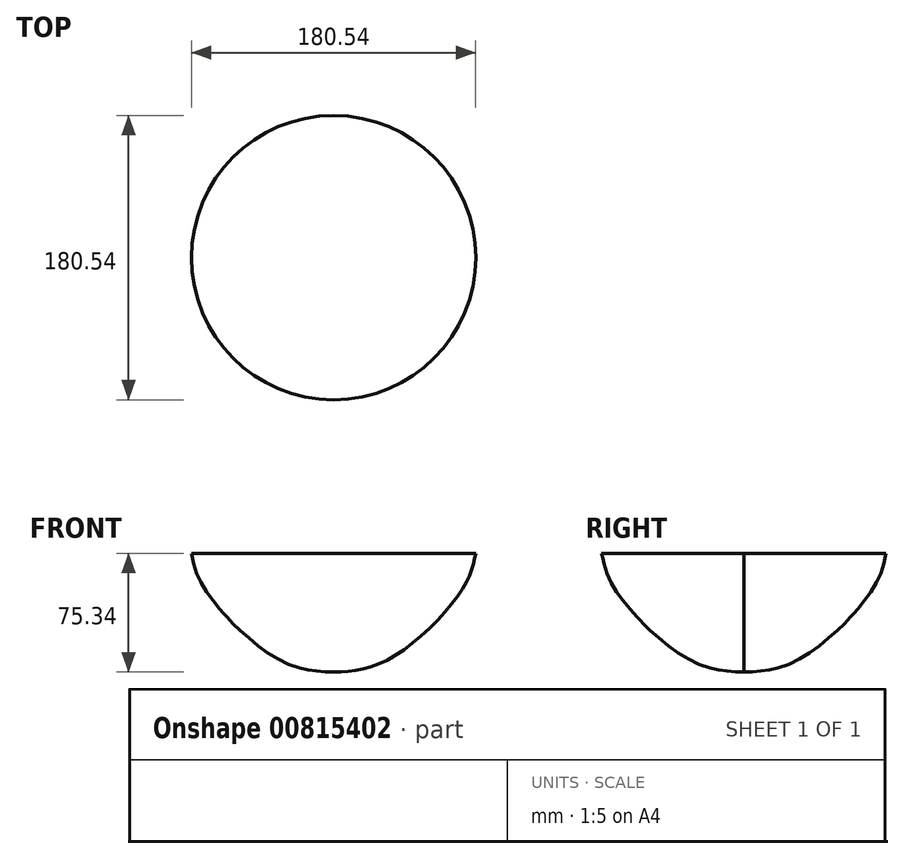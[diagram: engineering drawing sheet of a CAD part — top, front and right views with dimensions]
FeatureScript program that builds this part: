
annotation { "Feature Type Name" : "Feature", "Feature Type Description" : "" }
export const myFeature = defineFeature(function(context is Context, id is Id, definition is map)
    precondition{}
    {
        {
            var Q0;
            Q0=qCreatedBy(makeId("Front.planeOp"),FACE);
            var sketch = newSketch(context, id + "F0", { "sketchPlane" : qUnion([Q0])});
            skFitSpline(sketch, "E0", {"points": [v(0, 0) * mm, v(35.52, 8.33) * mm, v(82.2, 53.18) * mm, v(90.27, 75.34) * mm], "startDerivative": vector(106.17, 0) * mm, "endDerivative": vector(15.42, 77.78) * mm});
            skLineSegment(sketch, "E1", {"start": v(0, 0) * mm, "end": v(-42.95, 0) * mm, "construction": true});
            skLineSegment(sketch, "E2", {"start": v(0, 0) * mm, "end": v(0, 72.47) * mm, "construction": true});
            skSolve(sketch);
        }
        {
            var Q0;
            Q0 = qSketchRegion(id + "F0", true);
            var Q1;
            Q1=sQuery(id+"F0.wireOp",EDGE,"E0");
            var Q2;
            Q2=sQuery(id+"F0.wireOp",EDGE,"E2");
            revolve(context, id + "F1", {"bodyType" : ToolBodyType.SURFACE, "surfaceOperationType" : NewSurfaceOperationType.NEW, "entities" : qUnion([Q0]), "surfaceEntities" : qUnion([Q1]), "axis" : qUnion([Q2]), "revolveType" : RevolveType.FULL});
        }
    });
